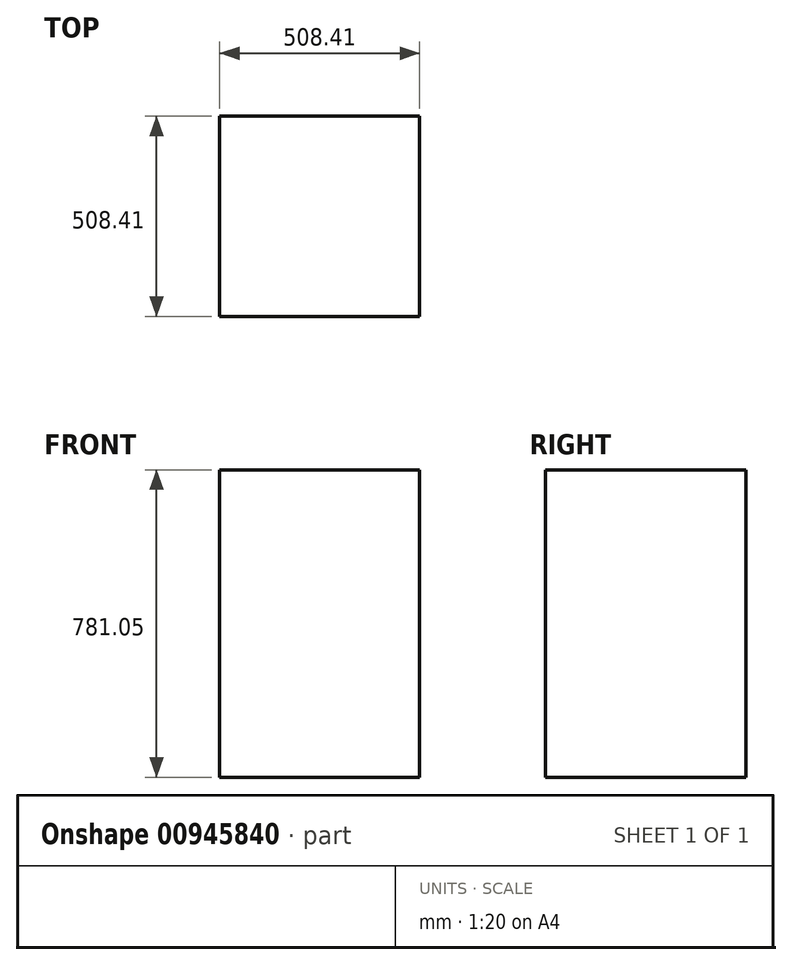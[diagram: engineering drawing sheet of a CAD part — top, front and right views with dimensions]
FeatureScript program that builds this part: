
annotation { "Feature Type Name" : "Feature", "Feature Type Description" : "" }
export const myFeature = defineFeature(function(context is Context, id is Id, definition is map)
    precondition{}
    {
        {
            var Q0;
            Q0=qCreatedBy(makeId("Top.planeOp"),FACE);
            var sketch = newSketch(context, id + "F0", { "sketchPlane" : qUnion([Q0])});
            skLineSegment(sketch, "E0.bottom", {"start": v(-508.4, 508.4) * mm, "end": v(0, 508.4) * mm});
            skLineSegment(sketch, "E0.top", {"start": v(-508.4, 0) * mm, "end": v(0, 0) * mm});
            skLineSegment(sketch, "E0.left", {"start": v(-508.4, 508.4) * mm, "end": v(-508.4, 0) * mm});
            skLineSegment(sketch, "E0.right", {"start": v(0, 508.4) * mm, "end": v(0, 0) * mm});
            skSolve(sketch);
        }
        {
            var Q0;
            Q0=makeQuery(id+"F0.imprint","IMPRINT",FACE,{"disambiguationData":[TD([[makeQuery(id+"F0.imprint","IMPRINT",EDGE,{"derivedFrom":sQuery(id+"F0.wireOp",EDGE,"E0.bottom")}),-1.0]])]});
            extrude(context, id + "F1", {"entities" : qUnion([Q0]), "depth" : 781.05 * mm, "offsetDistance" : 25.4 * mm});
        }
    });
